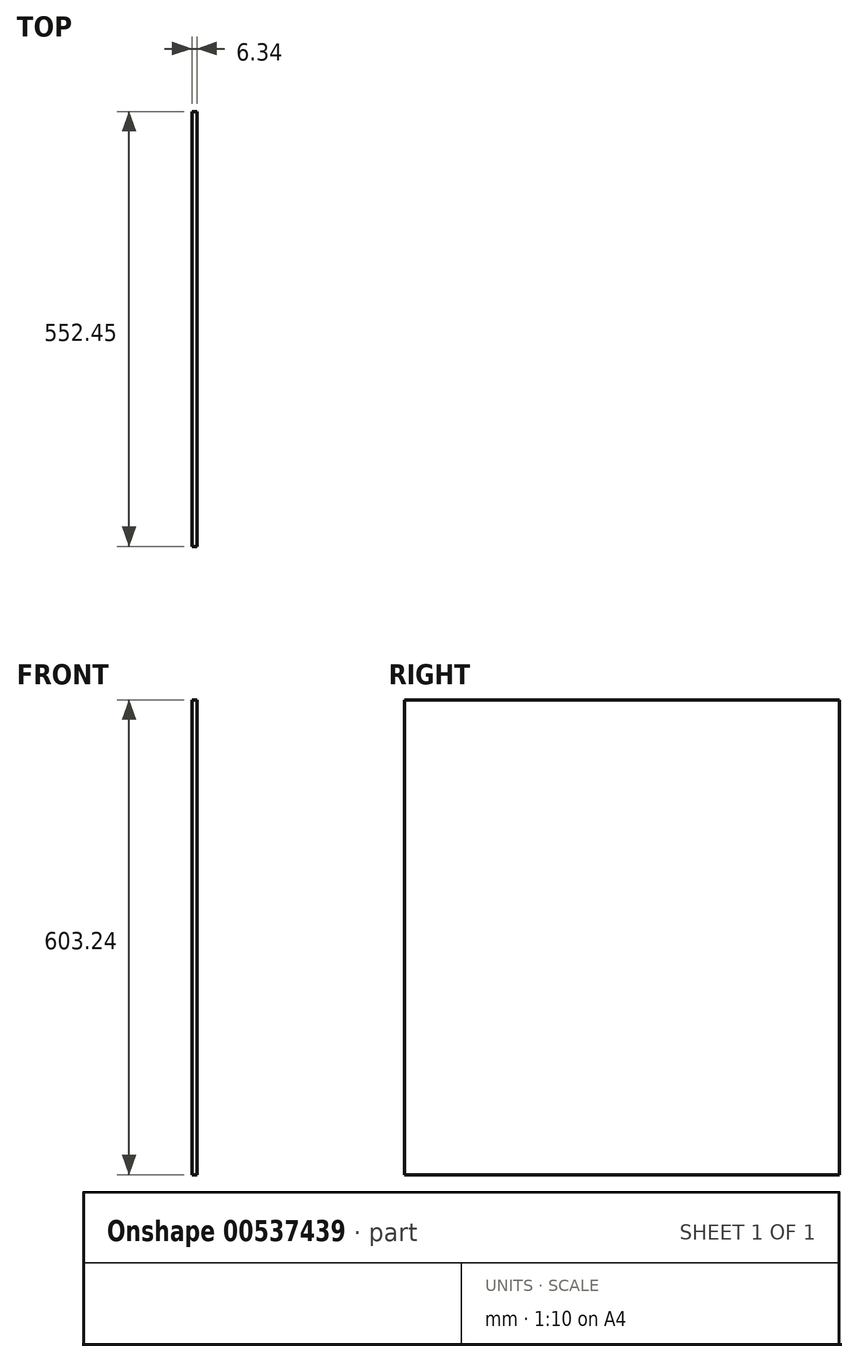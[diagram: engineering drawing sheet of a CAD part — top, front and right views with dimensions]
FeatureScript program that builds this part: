
annotation { "Feature Type Name" : "Feature", "Feature Type Description" : "" }
export const myFeature = defineFeature(function(context is Context, id is Id, definition is map)
    precondition{}
    {
        {
            var Q0;
            Q0=qCreatedBy(makeId("Front.planeOp"),FACE);
            var sketch = newSketch(context, id + "F0", { "sketchPlane" : qUnion([Q0])});
            skLineSegment(sketch, "E0.bottom", {"start": v(3.17, 301.63) * mm, "end": v(-3.18, 301.63) * mm});
            skLineSegment(sketch, "E0.top", {"start": v(3.18, -301.63) * mm, "end": v(-3.17, -301.63) * mm});
            skLineSegment(sketch, "E0.left", {"start": v(3.17, 301.63) * mm, "end": v(3.18, -301.63) * mm});
            skLineSegment(sketch, "E0.right", {"start": v(-3.18, 301.63) * mm, "end": v(-3.17, -301.63) * mm});
            skPoint(sketch, "E0.middle", {"position": v(0, 0) * mm});
            skSolve(sketch);
        }
        {
            var Q0;
            Q0 = qSketchRegion(id + "F0", true);
            extrude(context, id + "F1", {"entities" : qUnion([Q0]), "depth" : 552.45 * mm, "offsetDistance" : 25.4 * mm});
        }
    });
